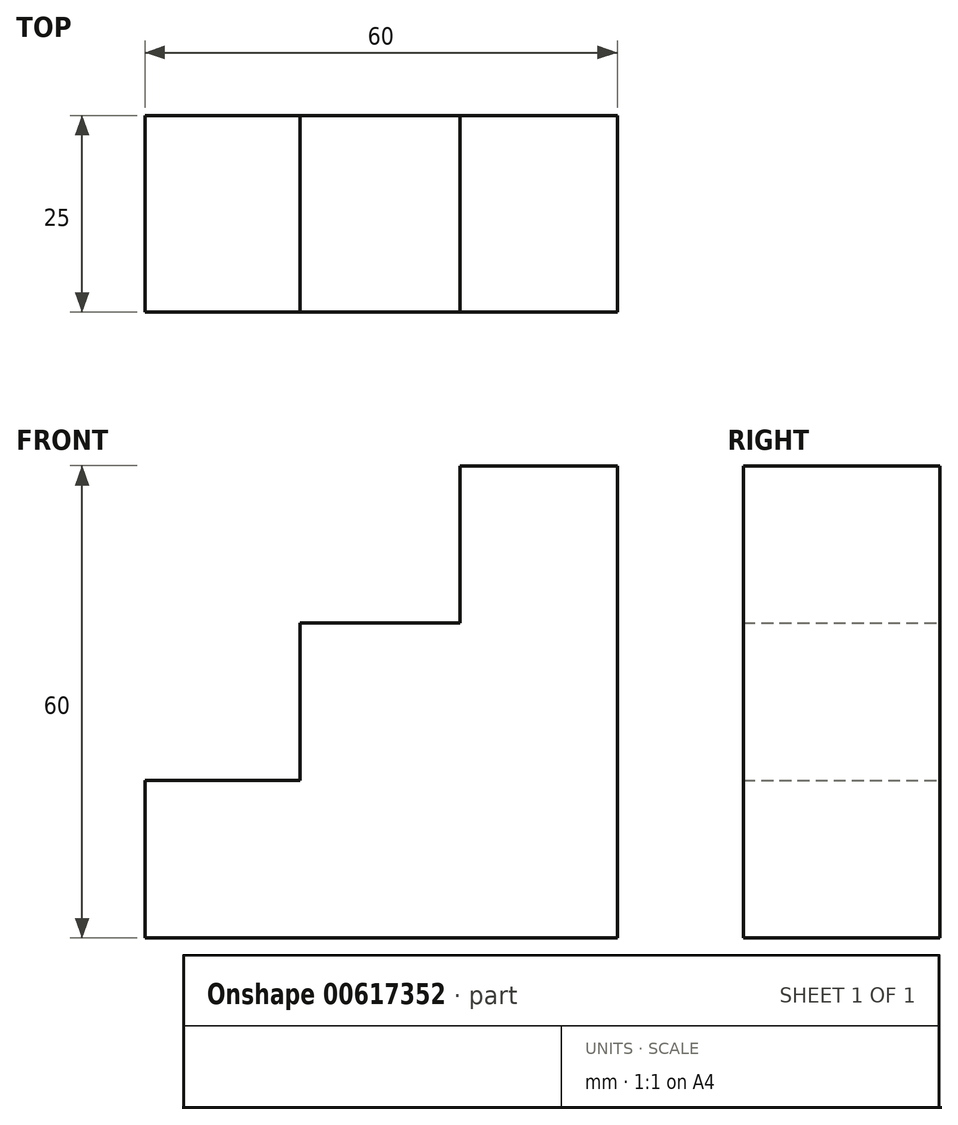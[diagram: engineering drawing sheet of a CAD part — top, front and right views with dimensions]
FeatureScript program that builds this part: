
annotation { "Feature Type Name" : "Feature", "Feature Type Description" : "" }
export const myFeature = defineFeature(function(context is Context, id is Id, definition is map)
    precondition{}
    {
        {
            var Q0;
            Q0=qCreatedBy(makeId("Front.planeOp"),FACE);
            var sketch = newSketch(context, id + "F0", { "sketchPlane" : qUnion([Q0])});
            skLineSegment(sketch, "E0", {"start": v(-20.66, -38.1) * mm, "end": v(39.34, -38.1) * mm});
            skLineSegment(sketch, "E1", {"start": v(39.34, -38.1) * mm, "end": v(39.34, -18.1) * mm});
            skLineSegment(sketch, "E2", {"start": v(39.34, -18.1) * mm, "end": v(-20.66, -18.1) * mm});
            skLineSegment(sketch, "E3", {"start": v(-20.66, -18.1) * mm, "end": v(-20.66, -38.1) * mm});
            skLineSegment(sketch, "E4", {"start": v(39.34, -18.1) * mm, "end": v(39.34, 1.9) * mm});
            skLineSegment(sketch, "E5", {"start": v(39.34, 1.9) * mm, "end": v(-0.97, 1.9) * mm});
            skLineSegment(sketch, "E6", {"start": v(-0.97, 1.9) * mm, "end": v(-0.97, -18.1) * mm});
            skLineSegment(sketch, "E7", {"start": v(39.34, 1.9) * mm, "end": v(39.34, 21.9) * mm});
            skLineSegment(sketch, "E8", {"start": v(39.34, 21.9) * mm, "end": v(19.34, 21.9) * mm});
            skLineSegment(sketch, "E9", {"start": v(19.34, 21.9) * mm, "end": v(19.34, 1.9) * mm});
            skSolve(sketch);
        }
        {
            var Q0;
            Q0 = qSketchRegion(id + "F0", true);
            extrude(context, id + "F1", {"entities" : qUnion([Q0]), "depth" : 25 * mm, "offsetDistance" : 25 * mm});
        }
    });
